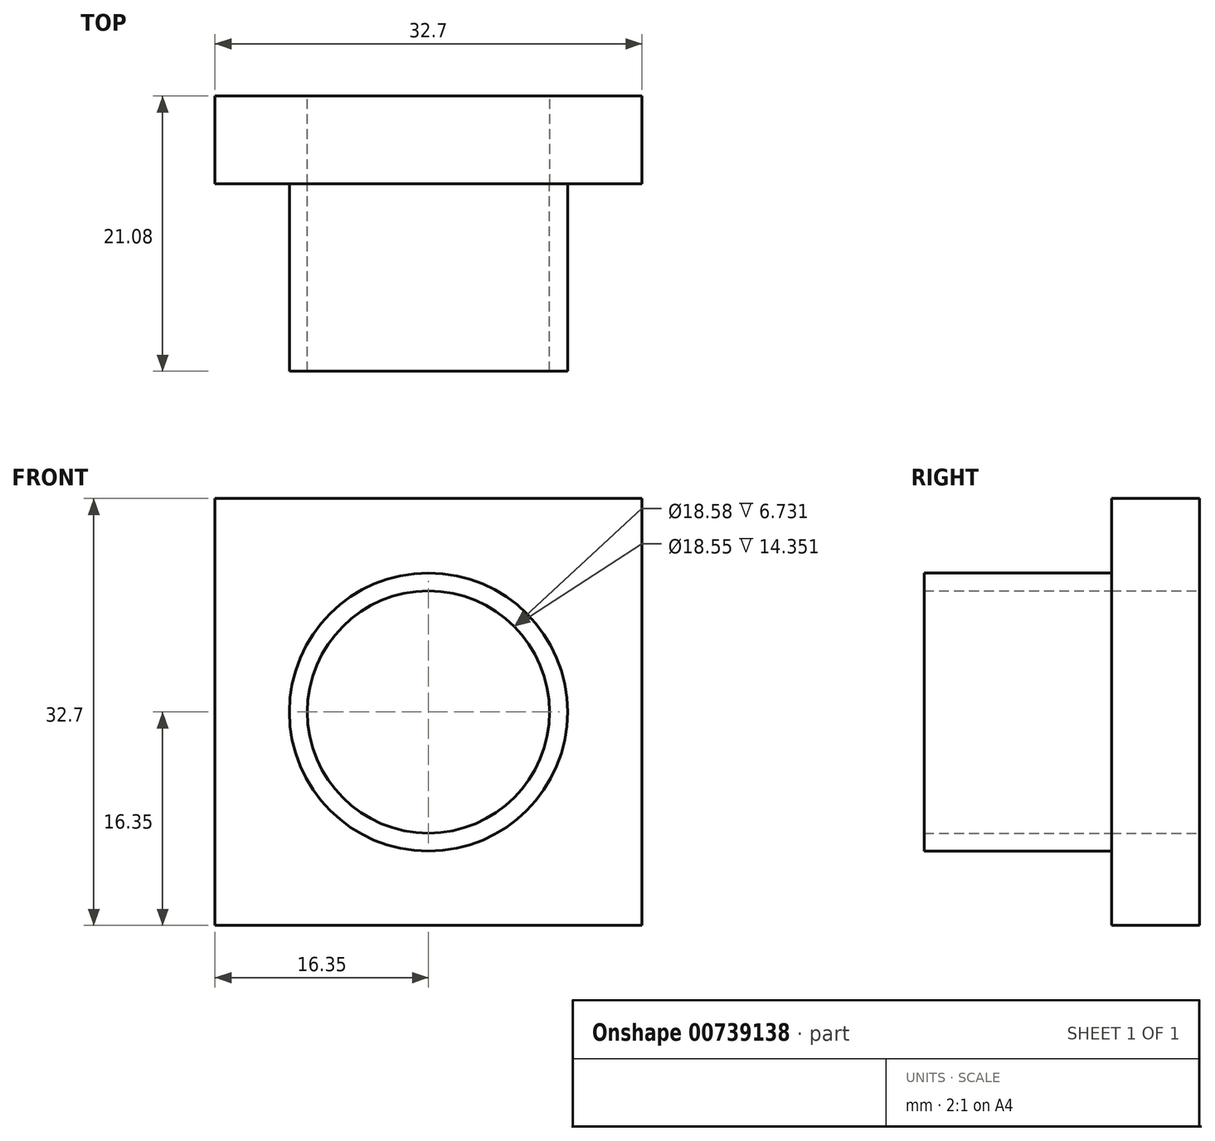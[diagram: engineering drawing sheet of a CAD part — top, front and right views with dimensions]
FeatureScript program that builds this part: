
annotation { "Feature Type Name" : "Feature", "Feature Type Description" : "" }
export const myFeature = defineFeature(function(context is Context, id is Id, definition is map)
    precondition{}
    {
        {
            var Q0;
            Q0=qCreatedBy(makeId("Front.planeOp"),FACE);
            var sketch = newSketch(context, id + "F0", { "sketchPlane" : qUnion([Q0])});
            skLineSegment(sketch, "E0", {"start": v(0, -16.35) * mm, "end": v(0, -16.35) * mm});
            skLineSegment(sketch, "E1", {"start": v(-16.35, 0) * mm, "end": v(-16.35, -16.35) * mm});
            skLineSegment(sketch, "E2", {"start": v(-16.35, -16.35) * mm, "end": v(0, -16.35) * mm});
            skLineSegment(sketch, "E3", {"start": v(16.35, 0) * mm, "end": v(16.35, -16.35) * mm});
            skLineSegment(sketch, "E4", {"start": v(16.35, -16.35) * mm, "end": v(0, -16.35) * mm});
            skLineSegment(sketch, "E5", {"start": v(-16.35, 0) * mm, "end": v(-16.35, 16.35) * mm});
            skLineSegment(sketch, "E6", {"start": v(-16.35, 16.35) * mm, "end": v(0, 16.35) * mm});
            skLineSegment(sketch, "E7", {"start": v(0, 16.35) * mm, "end": v(16.35, 16.35) * mm});
            skLineSegment(sketch, "E8", {"start": v(16.35, 16.35) * mm, "end": v(16.35, 0) * mm});
            skCircle(sketch, "E9", {"center": v(0, 0) * mm, "radius": 9.3 * mm});
            skSolve(sketch);
        }
        {
            var Q0;
            Q0 = qSketchRegion(id + "F0", true);
            var Q1;
            Q1=makeQuery(id+"F0.imprint","IMPRINT",FACE,{"disambiguationData":[TD([[makeQuery(id+"F0.imprint","IMPRINT",EDGE,{"derivedFrom":sQuery(id+"F0.wireOp",EDGE,"E1")}),1.0]])]});
            extrude(context, id + "F1", {"entities" : qUnion([Q0, Q1]), "depth" : 6.73 * mm, "offsetDistance" : 25.4 * mm});
        }
        {
            var Q0;
            Q0=makeQuery(id+"F1.opExtrude","CAP_FACE",FACE,{"disambiguationData":[OSD([sQuery(id+"F0.wireOp",EDGE,"E1"),sQuery(id+"F0.wireOp",EDGE,"E2"),sQuery(id+"F0.wireOp",EDGE,"E3"),sQuery(id+"F0.wireOp",EDGE,"E4"),sQuery(id+"F0.wireOp",EDGE,"E5"),sQuery(id+"F0.wireOp",EDGE,"E6"),sQuery(id+"F0.wireOp",EDGE,"E7"),sQuery(id+"F0.wireOp",EDGE,"E8"),sQuery(id+"F0.wireOp",EDGE,"E9")])],"isStart":false});
            var sketch = newSketch(context, id + "F2", { "sketchPlane" : qUnion([Q0])});
            skCircle(sketch, "E10", {"center": v(0, 0) * mm, "radius": 9.28 * mm});
            skCircle(sketch, "E11", {"center": v(0, 0) * mm, "radius": 10.66 * mm});
            skSolve(sketch);
        }
        {
            var Q0;
            Q0 = qSketchRegion(id + "F2", true);
            extrude(context, id + "F3", {"entities" : qUnion([Q0]), "operationType" : NewBodyOperationType.ADD, "depth" : 14.35 * mm, "offsetDistance" : 25.4 * mm});
        }
    });
